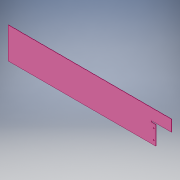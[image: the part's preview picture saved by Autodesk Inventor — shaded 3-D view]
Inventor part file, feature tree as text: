
AUTODESK INVENTOR PART (.ipt)
format: ipt  version: 2018 (Build 220112000, 112)  size: 117,760 bytes
history: native  units: mm
features: extrude x3, sketch x3
ambient origin geometry x8: Origin, YZ Plane, XZ Plane, XY Plane, X Axis, Y Axis, Z Axis, Center Point
bodies: Solid1 (feature_tree)
feature tree (6):
  extrude  "Extrusion1"  Depth=150.0mm
  extrude  "Extrusion3"  Depth=20.0mm
  extrude  "Extrusion4"  Depth=95.0mm
  sketch  "Sketch1"  dims[d0=710.0mm d1=150.0mm]
  sketch  "Sketch2"  dims[d2=1.6mm d3=0.0mm d6=20.0mm]
  sketch  "Sketch3"  dims[d7=60.0mm d10=5.0mm d11=5.0mm d12=50.0mm d13=20.0mm d14=1.6mm d15=0.0mm d16=54.0mm d17=1.6mm d18=95.0mm d19=0.0mm]
